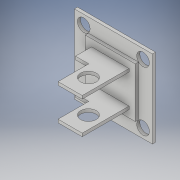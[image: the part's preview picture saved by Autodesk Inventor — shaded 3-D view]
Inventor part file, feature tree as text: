
AUTODESK INVENTOR PART (.ipt)
format: ipt  version: 2018 (Build 220112000, 112)  size: 180,736 bytes
history: native  units: in
note: dims shown in document units (in); Inventor stores cm internally (conversion verified against a paired STEP export)
features: extrude x6, sketch x6
ambient origin geometry x8: Origin, YZ Plane, XZ Plane, XY Plane, X Axis, Y Axis, Z Axis, Center Point
bodies: Solid1 (feature_tree)
feature tree (12):
  extrude  "Extrusion1"  Depth=1.25in
  extrude  "Extrusion2"  Depth=0.225in
  extrude  "Extrusion3"  Depth=0.225in
  extrude  "Extrusion4"  Depth=0.05in TaperAngle=0.0deg
  extrude  "Extrusion5"  Depth=0.75in
  extrude  "Extrusion6"  Depth=0.1145in TaperAngle=0.0deg
  sketch  "Sketch1"  dims[d0=1.25in d1=1.25in]
  sketch  "Sketch2"  dims[d2=0.05in d3=0.0in d4=0.225in]
  sketch  "Sketch3"  dims[d5=0.225in d6=0.225in]
  sketch  "Sketch4"  dims[d7=0.225in d8=0.05in d9=0.0in]
  sketch  "Sketch5"  dims[d18=0.75in d19=0.0in d20=0.25in]
  sketch  "Sketch6"  dims[d21=0.3in d22=5.0in d23=0.0in d24=0.2031in d28=0.2031in d29=0.15in d30=0.15in d31=0.15in d32=0.15in d33=0.2031in d34=0.15in d35=0.15in d36=0.2031in d37=0.15in d38=0.15in d42=0.5in d43=0.0in d44=0.4in d45=4.0in d46=0.0in d48=0.05in d49=0.471in d50=0.05in d54=0.1in d55=0.1in d56=0.1in d57=0.1in d58=0.1145in d59=0.115in]
